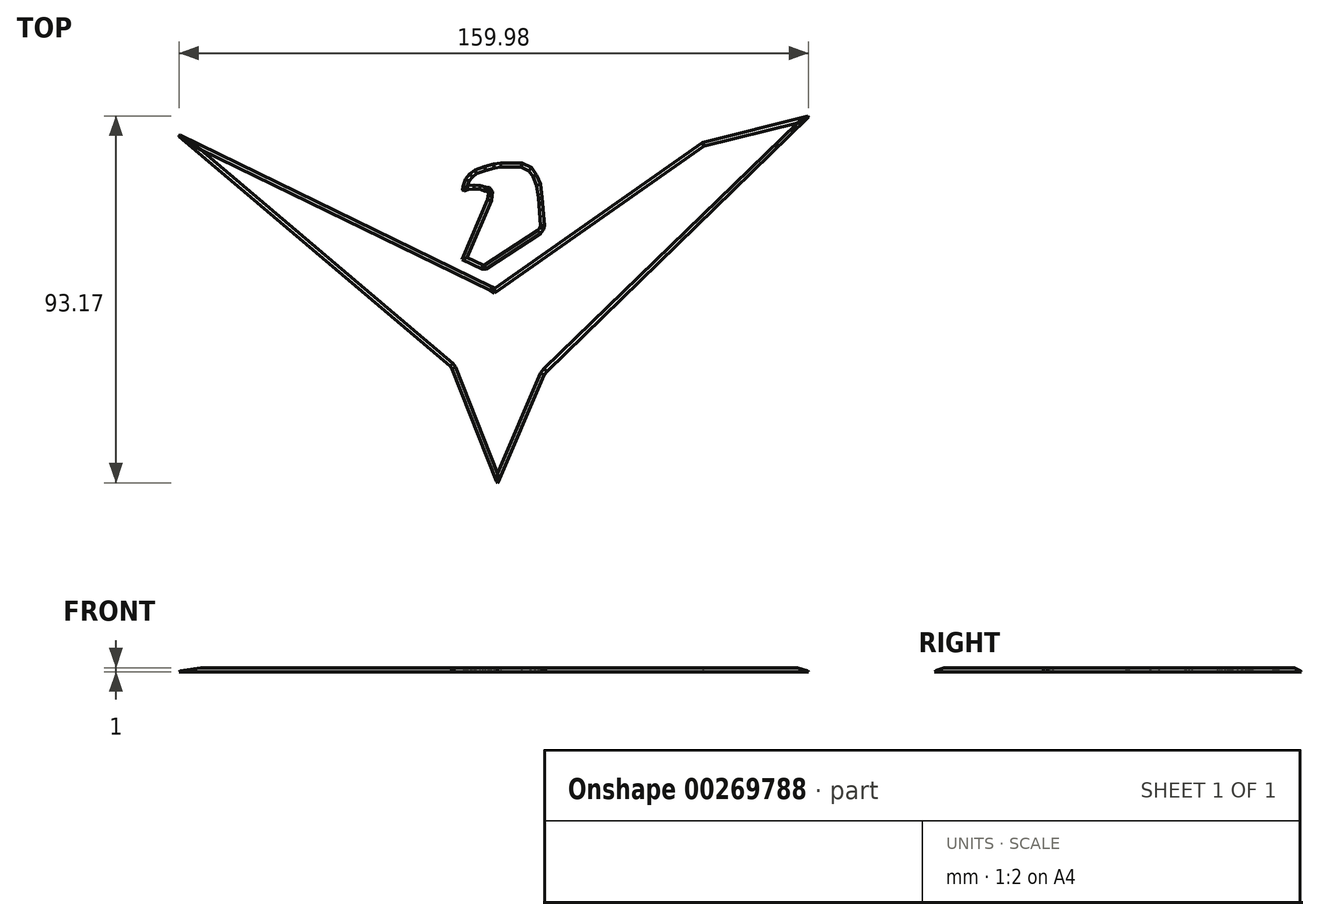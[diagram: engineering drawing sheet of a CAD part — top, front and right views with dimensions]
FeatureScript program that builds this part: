
annotation { "Feature Type Name" : "Feature", "Feature Type Description" : "" }
export const myFeature = defineFeature(function(context is Context, id is Id, definition is map)
    precondition{}
    {
        {
            var Q0;
            Q0=qCreatedBy(makeId("Top.planeOp"),FACE);
            var sketch = newSketch(context, id + "F0", { "sketchPlane" : qUnion([Q0])});
            skLineSegment(sketch, "E0", {"start": v(-50.02, 38.82) * mm, "end": v(-50.08, 38.6) * mm});
            skLineSegment(sketch, "E1", {"start": v(-50.08, 38.6) * mm, "end": v(18.76, -19.7) * mm});
            skLineSegment(sketch, "E2", {"start": v(18.76, -19.7) * mm, "end": v(19.26, -20.47) * mm});
            skLineSegment(sketch, "E3", {"start": v(19.26, -20.47) * mm, "end": v(30.56, -49.03) * mm});
            skLineSegment(sketch, "E4", {"start": v(30.56, -49.03) * mm, "end": v(30.84, -49.38) * mm});
            skLineSegment(sketch, "E5", {"start": v(30.84, -49.38) * mm, "end": v(30.96, -49.28) * mm});
            skLineSegment(sketch, "E6", {"start": v(30.96, -49.28) * mm, "end": v(42.67, -22.02) * mm});
            skLineSegment(sketch, "E7", {"start": v(42.67, -22.02) * mm, "end": v(43.39, -21.04) * mm});
            skLineSegment(sketch, "E8", {"start": v(43.39, -21.04) * mm, "end": v(109.8, 43.37) * mm});
            skLineSegment(sketch, "E9", {"start": v(109.8, 43.37) * mm, "end": v(109.9, 43.61) * mm});
            skLineSegment(sketch, "E10", {"start": v(109.9, 43.61) * mm, "end": v(109.8, 43.79) * mm});
            skLineSegment(sketch, "E11", {"start": v(109.8, 43.79) * mm, "end": v(82.88, 37.08) * mm});
            skLineSegment(sketch, "E12", {"start": v(82.88, 37.08) * mm, "end": v(30.56, 0.32) * mm});
            skLineSegment(sketch, "E13", {"start": v(30.56, 0.32) * mm, "end": v(30.1, 0) * mm});
            skLineSegment(sketch, "E14", {"start": v(30.1, 0) * mm, "end": v(29.5, 0.35) * mm});
            skLineSegment(sketch, "E15", {"start": v(29.5, 0.35) * mm, "end": v(-49.83, 38.92) * mm});
            skLineSegment(sketch, "E16", {"start": v(-49.83, 38.92) * mm, "end": v(-50.02, 38.82) * mm});
            skLineSegment(sketch, "E17", {"start": v(21.85, 7.38) * mm, "end": v(26.9, 4.93) * mm});
            skLineSegment(sketch, "E18", {"start": v(26.9, 4.93) * mm, "end": v(27.9, 4.93) * mm});
            skLineSegment(sketch, "E19", {"start": v(27.9, 4.93) * mm, "end": v(41.76, 13.99) * mm});
            skLineSegment(sketch, "E20", {"start": v(41.76, 13.99) * mm, "end": v(42.59, 14.97) * mm});
            skLineSegment(sketch, "E21", {"start": v(42.59, 14.97) * mm, "end": v(42.82, 15.94) * mm});
            skLineSegment(sketch, "E22", {"start": v(42.82, 15.94) * mm, "end": v(42.22, 23.07) * mm});
            skLineSegment(sketch, "E23", {"start": v(42.22, 23.07) * mm, "end": v(41.76, 26.47) * mm});
            skLineSegment(sketch, "E24", {"start": v(41.76, 26.47) * mm, "end": v(40.8, 28.87) * mm});
            skLineSegment(sketch, "E25", {"start": v(40.8, 28.87) * mm, "end": v(39.54, 30.66) * mm});
            skLineSegment(sketch, "E26", {"start": v(39.54, 30.66) * mm, "end": v(38, 31.41) * mm});
            skLineSegment(sketch, "E27", {"start": v(38, 31.41) * mm, "end": v(37.1, 31.85) * mm});
            skLineSegment(sketch, "E28", {"start": v(37.1, 31.85) * mm, "end": v(31.69, 31.85) * mm});
            skLineSegment(sketch, "E29", {"start": v(31.69, 31.85) * mm, "end": v(29.91, 31.56) * mm});
            skLineSegment(sketch, "E30", {"start": v(29.91, 31.56) * mm, "end": v(27.54, 30.94) * mm});
            skLineSegment(sketch, "E31", {"start": v(27.54, 30.94) * mm, "end": v(25.12, 30.04) * mm});
            skLineSegment(sketch, "E32", {"start": v(25.12, 30.04) * mm, "end": v(23.78, 29.1) * mm});
            skLineSegment(sketch, "E33", {"start": v(23.78, 29.1) * mm, "end": v(22.76, 27.77) * mm});
            skLineSegment(sketch, "E34", {"start": v(22.76, 27.77) * mm, "end": v(22.07, 25.9) * mm});
            skLineSegment(sketch, "E35", {"start": v(22.07, 25.9) * mm, "end": v(22.01, 24.95) * mm});
            skLineSegment(sketch, "E36", {"start": v(22.01, 24.95) * mm, "end": v(22.32, 24.7) * mm});
            skLineSegment(sketch, "E37", {"start": v(22.32, 24.7) * mm, "end": v(23.36, 25.13) * mm});
            skLineSegment(sketch, "E38", {"start": v(23.36, 25.13) * mm, "end": v(24.91, 25.32) * mm});
            skLineSegment(sketch, "E39", {"start": v(24.91, 25.32) * mm, "end": v(26.26, 25.2) * mm});
            skLineSegment(sketch, "E40", {"start": v(26.26, 25.2) * mm, "end": v(27.62, 24.8) * mm});
            skLineSegment(sketch, "E41", {"start": v(27.62, 24.8) * mm, "end": v(28.25, 24.67) * mm});
            skLineSegment(sketch, "E42", {"start": v(28.25, 24.67) * mm, "end": v(28.6, 24.27) * mm});
            skLineSegment(sketch, "E43", {"start": v(28.6, 24.27) * mm, "end": v(28.51, 23.55) * mm});
            skLineSegment(sketch, "E44", {"start": v(28.51, 23.55) * mm, "end": v(28.39, 22.62) * mm});
            skLineSegment(sketch, "E45", {"start": v(28.39, 22.62) * mm, "end": v(21.85, 7.38) * mm});
            skSolve(sketch);
        }
        {
            var Q0;
            Q0 = qSketchRegion(id + "F0", true);
            extrude(context, id + "F1", {"entities" : qUnion([Q0]), "offsetDistance" : 25 * mm, "depth" : 1 * mm, "hasDraft" : true, "draftAngle" : 45 * degree, "draftPullDirection" : true});
        }
    });
